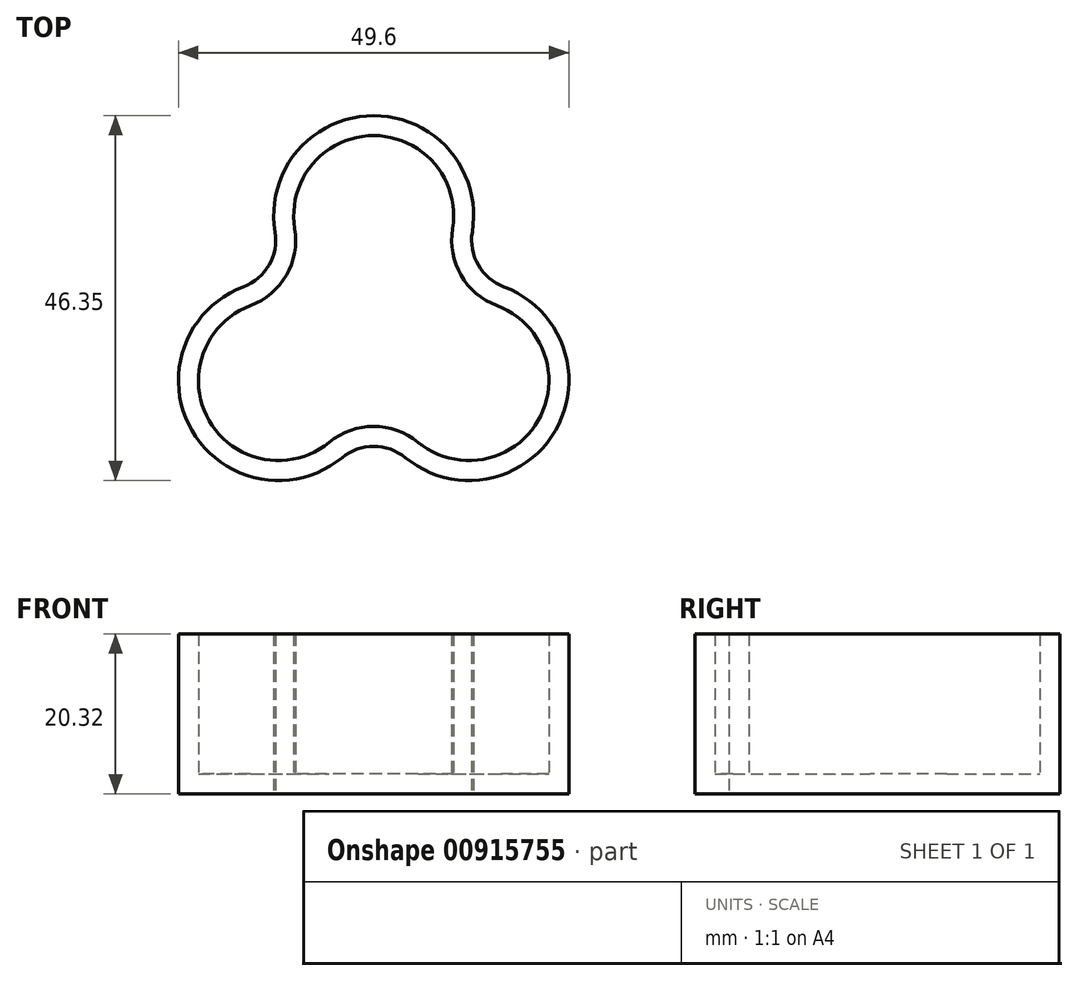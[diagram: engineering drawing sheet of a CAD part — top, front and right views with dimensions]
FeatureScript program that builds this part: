
annotation { "Feature Type Name" : "Feature", "Feature Type Description" : "" }
export const myFeature = defineFeature(function(context is Context, id is Id, definition is map)
    precondition{}
    {
        {
            var Q0;
            Q0=qCreatedBy(makeId("Top.planeOp"),FACE);
            var sketch = newSketch(context, id + "F0", { "sketchPlane" : qUnion([Q0])});
            skLineSegment(sketch, "E0", {"start": v(0, 0) * mm, "end": v(-12.1, -6.98) * mm, "construction": true});
            skLineSegment(sketch, "E1", {"start": v(0, 0) * mm, "end": v(12.1, -6.98) * mm, "construction": true});
            skLineSegment(sketch, "E2", {"start": v(0, 13.97) * mm, "end": v(0, 0) * mm, "construction": true});
            skArc(sketch, "E3", {"start": v(4.03, -16.8) * mm, "mid": v(23.1, -13.33) * mm, "end": v(16.56, 4.9) * mm});
            skLineSegment(sketch, "E4", {"start": v(-2.7, 1.56) * mm, "end": v(-2.7, 1.56) * mm});
            skArc(sketch, "E5", {"start": v(-16.56, 4.9) * mm, "mid": v(-23.1, -13.33) * mm, "end": v(-4.03, -16.8) * mm});
            skLineSegment(sketch, "E6", {"start": v(9.4, 5.42) * mm, "end": v(9.4, 5.42) * mm});
            skArc(sketch, "E7.trimOffspring", {"start": v(12.53, 11.9) * mm, "mid": v(0, 26.67) * mm, "end": v(-12.53, 11.9) * mm});
            skPoint(sketch, "E8.visualSharp", {"position": v(9.4, 5.42) * mm});
            skArc(sketch, "E8.filletArc", {"start": v(12.53, 11.9) * mm, "mid": v(13.3, 7.68) * mm, "end": v(16.56, 4.9) * mm});
            skArc(sketch, "E9.filletArc", {"start": v(4.03, -16.8) * mm, "mid": v(0, -15.35) * mm, "end": v(-4.03, -16.8) * mm});
            skPoint(sketch, "E10.visualSharp", {"position": v(-9.4, 5.42) * mm});
            skArc(sketch, "E10.filletArc", {"start": v(-16.56, 4.9) * mm, "mid": v(-13.3, 7.68) * mm, "end": v(-12.53, 11.9) * mm});
            skSolve(sketch);
        }
        {
            var Q0;
            Q0 = qSketchRegion(id + "F0", true);
            extrude(context, id + "F1", {"entities" : qUnion([Q0]), "depth" : 20.32 * mm, "offsetDistance" : 25.4 * mm});
        }
        {
            var Q0;
            Q0=makeQuery(id+"F1.opExtrude","CAP_FACE",FACE,{"disambiguationData":[OSD([sQuery(id+"F0.wireOp",EDGE,"E3"),sQuery(id+"F0.wireOp",EDGE,"E5"),sQuery(id+"F0.wireOp",EDGE,"E7.trimOffspring"),sQuery(id+"F0.wireOp",EDGE,"E8.filletArc"),sQuery(id+"F0.wireOp",EDGE,"E9.filletArc"),sQuery(id+"F0.wireOp",EDGE,"E10.filletArc")])],"isStart":false});
            shell(context, id + "F2", {"entities" : qUnion([Q0]), "thickness" : 2.54 * mm});
        }
    });
